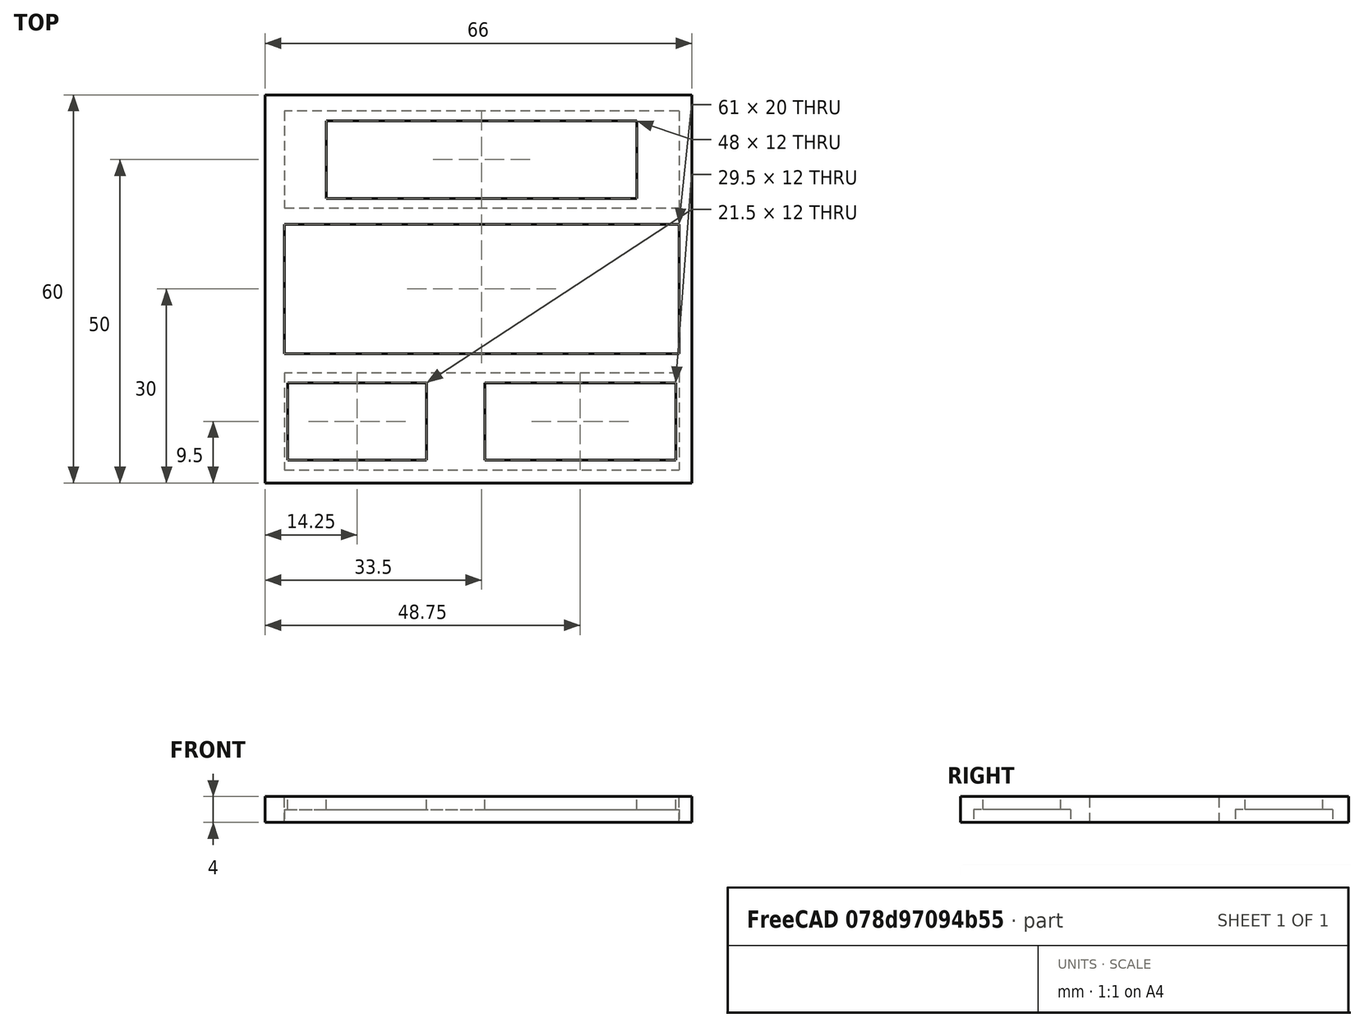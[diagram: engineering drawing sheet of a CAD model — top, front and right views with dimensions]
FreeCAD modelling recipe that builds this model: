
FCSTD DOCUMENT  (FreeCAD 0.17R13522 (Git))
Label: test_panel_display1
License: CreativeCommons Attribution-ShareAlike
LicenseURL: http://creativecommons.org/licenses/by-sa/4.0/
objects: Part::Feature×51, Part::Fuse×42, Part::Cut×22, Part::Part2DObjectPython×10, Part::Box×9, Part::FeaturePython×4, Part::Extrusion×1, App::DocumentObjectGroup×1
note: 139 computed .brp shape members not serialized (recipe doc carries the construction recipe); baked Part::Feature solids carry a one-line shape summary decoded from their .brp

FEATURE [Part::Box] Box  label="base principal"
  AttacherType = Attacher::AttachEngine3D
  Height = 4
  Length = 280
  Placement = pos=(0,0,-4) rot=(0,0,1;0rad)
  Width = 210
FEATURE [Part::Feature] Fusion008001001  label="perforador encoder"
  Placement = pos=(17,17,-6) rot=(1,0,0;3.14159rad)
  shape: bbox 82.5 x 15 x 10 mm, 18 faces (baked)
FEATURE [Part::Feature] Fusion008001001001  label="perforador active 1"
  Placement = pos=(17,98,-6) rot=(1,0,0;3.14159rad)
  shape: bbox 82.5 x 15 x 10 mm, 18 faces (baked)
FEATURE [Part::Feature] Fusion008001001002  label="perforador active 2"
  Placement = pos=(17,57.5,-6) rot=(1,0,0;3.14159rad)
  shape: bbox 82.5 x 15 x 10 mm, 18 faces (baked)
FEATURE [Part::Feature] Fusion008001001003  label="perforador standby 1"
  Placement = pos=(136,98,-6) rot=(1,0,0;3.14159rad)
  shape: bbox 82.5 x 15 x 10 mm, 18 faces (baked)
FEATURE [Part::Feature] Fusion008001001004  label="perforador standby 2"
  Placement = pos=(136,57.5,-6) rot=(1,0,0;3.14159rad)
  shape: bbox 82.5 x 15 x 10 mm, 18 faces (baked)
FEATURE [Part::Cut] Cut
  Base = -> Box
  Refine = true
  Tool = -> Fusion008001001
FEATURE [Part::Cut] Cut001
  Base = -> Cut
  Refine = true
  Tool = -> Fusion008001001001
FEATURE [Part::Cut] Cut002
  Base = -> Cut001
  Refine = true
  Tool = -> Fusion008001001002
FEATURE [Part::Cut] Cut003
  Base = -> Cut002
  Refine = true
  Tool = -> Fusion008001001003
FEATURE [Part::Cut] Cut004  label="base con 7 segmentos sin frente perforado"
  Base = -> Cut003
  Refine = true
  Tool = -> Fusion008001001004
FEATURE [Part::Feature] BooleanFragments001  label="perforador encoder izquierda"
  Placement = pos=(130,20.2,4) rot=(0,0,1;0rad)
  shape: bbox 45.2 x 30 x 10 mm, 34 faces, 4 solids (baked)
FEATURE [Part::Feature] BooleanFragments002  label="perforador encoder derecha"
  Placement = pos=(178,20.2,4) rot=(0,0,1;0rad)
  shape: bbox 45.2 x 30 x 10 mm, 34 faces, 4 solids (baked)
FEATURE [Part::Cut] Cut005
  Base = -> Cut004
  Refine = true
  Tool = -> BooleanFragments001
FEATURE [Part::Cut] Cut006  label="frente con agujeros displays y encoders transponder"
  Base = -> Cut005
  Refine = true
  Tool = -> BooleanFragments002
FEATURE [Part::Feature] Fusion005001  label="boton ident"
  Placement = pos=(203,14.2,1) rot=(0,0,1;0rad)
  shape: bbox 30 x 12 x 10 mm, 14 faces (baked)
FEATURE [Part::Cut] Cut007
  Base = -> Cut006
  Refine = true
  Tool = -> Fusion005001
FEATURE [Part::Part2DObjectPython] Line009  # Draft 2D object (typed FeaturePython)
  ChamferSize = 0
  Closed = false
  End = (270.847,20.2,0)
  FilletRadius = 0
  Length = 35.3471
  MakeFace = false
  Points = (2) [(235.5,20.2,0),(270.847,20.2,0)]
  Start = (235.5,20.2,0)
  Subdivisions = 0
FEATURE [Part::Part2DObjectPython] Circle  # Draft 2D object (typed FeaturePython)
  FirstAngle = 0
  LastAngle = 0
  MakeFace = false
  Placement = pos=(269.619,20.2,4) rot=(0,0,1;0rad)
  Radius = 4.75
FEATURE [Part::Part2DObjectPython] Circle001  # Draft 2D object (typed FeaturePython)
  FirstAngle = 0
  LastAngle = 0
  MakeFace = false
  Placement = pos=(259.67,20.2,0) rot=(0,0,1;0rad)
  Radius = 14
FEATURE [Part::Extrusion] Extrude
  Base = -> Circle
  Dir = (0,0,1)
  DirMode = 2
  FaceMakerClass = Part::FaceMakerBullseye
  LengthFwd = 10
  LengthRev = 0
  Placement = pos=(-10,0,-10) rot=(0,0,1;0rad)
  Solid = true
  Symmetric = false
FEATURE [Part::Part2DObjectPython] Line014  # Draft 2D object (typed FeaturePython)
  ChamferSize = 0
  Closed = false
  End = (248.272,28.2144,0)
  FilletRadius = 0
  Length = 13.696
  MakeFace = false
  Placement = pos=(-10,0,-4) rot=(0,0,1;0rad)
  Points = (2) [(269.378,20.2,4),(258.272,28.2144,4)]
  Start = (259.378,20.2,0)
  Subdivisions = 0
FEATURE [Part::Part2DObjectPython] Line015  # Draft 2D object (typed FeaturePython)
  ChamferSize = 0
  Closed = false
  End = (254.876,33.263,0)
  FilletRadius = 0
  Length = 13.7518
  MakeFace = false
  Placement = pos=(-10,0,-4) rot=(0,0,1;0rad)
  Points = (2) [(269.174,20.2,4),(264.876,33.263,4)]
  Start = (259.174,20.2,0)
  Subdivisions = 0
FEATURE [Part::Part2DObjectPython] Line016  # Draft 2D object (typed FeaturePython)
  ChamferSize = 0
  Closed = false
  End = (263.227,33.6931,0)
  FilletRadius = 0
  Length = 14.1488
  MakeFace = false
  Placement = pos=(-10,0,-4) rot=(0,0,1;0rad)
  Points = (2) [(268.97,20.2,4),(273.227,33.6931,4)]
  Start = (258.97,20.2,0)
  Subdivisions = 0
FEATURE [Part::Part2DObjectPython] Line017  # Draft 2D object (typed FeaturePython)
  ChamferSize = 0
  Closed = false
  End = (270.612,28.9289,0)
  FilletRadius = 0
  Length = 14.5511
  MakeFace = false
  Placement = pos=(-10,0,-4) rot=(0,0,1;0rad)
  Points = (2) [(268.97,20.2,4),(280.612,28.9289,4)]
  Start = (258.97,20.2,0)
  Subdivisions = 0
FEATURE [Part::Part2DObjectPython] Line  # Draft 2D object (typed FeaturePython)
  ChamferSize = 0
  Closed = true
  End = (269.619,20.2,0)
  FilletRadius = 0
  Length = 0
  MakeFace = false
  Points = (2) [(269.619,20.2,0),(269.619,20.2,0)]
  Start = (269.619,20.2,0)
  Subdivisions = 0
FEATURE [Part::Cut] Cut008  label="base con line inferior completa"
  Base = -> Cut007
  Refine = true
  Tool = -> Extrude
FEATURE [Part::Part2DObjectPython] Line019  # Draft 2D object (typed FeaturePython)
  ChamferSize = 0
  Closed = false
  End = (259.619,169.66,0)
  FilletRadius = 0
  Length = 149.46
  MakeFace = true
  Placement = pos=(-20,0,-10) rot=(0,0,1;0rad)
  Points = (2) [(279.619,20.2,10),(279.619,169.66,10)]
  Start = (259.619,20.2,0)
  Subdivisions = 0
FEATURE [Part::Part2DObjectPython] Line023  # Draft 2D object (typed FeaturePython)
  ChamferSize = 0
  Closed = false
  End = (270.85,61,0)
  FilletRadius = 0
  Length = 96.85
  MakeFace = false
  Points = (2) [(174,61,0),(270.85,61,0)]
  Start = (174,61,0)
  Subdivisions = 0
FEATURE [App::DocumentObjectGroup] Construction
  Group = -> [Line009,Circle001,Line014,Line015,Line016,Line017,Line,Line019,Line023]
FEATURE [Part::Feature] BooleanFragments003  label="perforador para comunication 1"
  Placement = pos=(251.8,102,3) rot=(0,0,1;3.14159rad)
  shape: bbox 45.2 x 30 x 10 mm, 34 faces, 4 solids (baked)
FEATURE [Part::Feature] BooleanFragments003001  label="perforador para comunication 2"
  Placement = pos=(251.8,61,4) rot=(0,0,1;3.14159rad)
  shape: bbox 45.2 x 30 x 10 mm, 34 faces, 4 solids (baked)
FEATURE [Part::Cut] Cut009
  Base = -> Cut008
  Refine = true
  Tool = -> BooleanFragments003001
FEATURE [Part::Cut] Cut010  label="panel sin botones y sin leds"
  Base = -> Cut009
  Refine = true
  Tool = -> BooleanFragments003
FEATURE [Part::Feature] Cut001001  label="the_spacer_1mm_inside"
  Placement = pos=(17,106.2,0) rot=(0.99953,0.030644,0;3.14159rad)
  shape: bbox 7 x 7 x 6 mm, 11 faces (baked)
FEATURE [Part::Fuse] Fusion
  Base = -> Cut010
  Refine = true
  Tool = -> Cut001001
FEATURE [Part::Fuse] Fusion008001001005
  Base = -> Fusion
  Refine = true
FEATURE [Part::Feature] Cut001001001  label="the_spacer_1mm_inside001"
  Placement = pos=(17,96.8,0) rot=(0.99953,0.030644,0;3.14159rad)
  shape: bbox 7 x 7 x 6 mm, 11 faces (baked)
FEATURE [Part::Fuse] Fusion008001001006
  Base = -> Fusion008001001005
  Refine = true
  Tool = -> Cut001001001
FEATURE [Part::Fuse] Fusion008001001007
  Placement = pos=(0,0,1) rot=(0,0,1;0rad)
  Refine = true
  Tool = -> Fusion008001001006
FEATURE [Part::Feature] Cut001001001001  label="the_spacer_1mm_inside002"
  Placement = pos=(17,56.3,0) rot=(0.99953,0.030644,0;3.14159rad)
  shape: bbox 7 x 7 x 6 mm, 11 faces (baked)
FEATURE [Part::Feature] Cut001001001002  label="the_spacer_1mm_inside003"
  Placement = pos=(17,65.7,0) rot=(0.99953,0.030644,0;3.14159rad)
  shape: bbox 7 x 7 x 6 mm, 11 faces (baked)
FEATURE [Part::Feature] Cut001001001002001  label="the_spacer_1mm_inside004"
  Placement = pos=(17,25.2,0) rot=(0.99953,0.030644,0;3.14159rad)
  shape: bbox 7 x 7 x 6 mm, 11 faces (baked)
FEATURE [Part::Feature] Cut001001001001001  label="the_spacer_1mm_inside005"
  Placement = pos=(17,15.8,0) rot=(0.99953,0.030644,0;3.14159rad)
  shape: bbox 7 x 7 x 6 mm, 11 faces (baked)
FEATURE [Part::Feature] Cut001001001002002  label="the_spacer_1mm_inside006"
  Placement = pos=(136,106.2,0) rot=(0.99953,0.030644,0;3.14159rad)
  shape: bbox 7 x 7 x 6 mm, 11 faces (baked)
FEATURE [Part::Feature] Cut001001001002003  label="the_spacer_1mm_inside007"
  Placement = pos=(136,96.8,0) rot=(0.99953,0.030644,0;3.14159rad)
  shape: bbox 7 x 7 x 6 mm, 11 faces (baked)
FEATURE [Part::Feature] Cut001001001002004  label="the_spacer_1mm_inside008"
  Placement = pos=(136,65.7,0) rot=(0.99953,0.030644,0;3.14159rad)
  shape: bbox 7 x 7 x 6 mm, 11 faces (baked)
FEATURE [Part::Feature] Cut001001001001002  label="the_spacer_1mm_inside009"
  Placement = pos=(136,56.3,0) rot=(0.99953,0.030644,0;3.14159rad)
  shape: bbox 7 x 7 x 6 mm, 11 faces (baked)
FEATURE [Part::Feature] Cut001001001001002001  label="the_spacer_1mm_inside010"
  Placement = pos=(93,65.7,0) rot=(0.99953,0.030644,0;3.14159rad)
  shape: bbox 7 x 7 x 6 mm, 11 faces (baked)
FEATURE [Part::Feature] Cut001001001002002001  label="the_spacer_1mm_inside011"
  Placement = pos=(93,106.2,0) rot=(0.99953,0.030644,0;3.14159rad)
  shape: bbox 7 x 7 x 6 mm, 11 faces (baked)
FEATURE [Part::Feature] Cut001001001002003001  label="the_spacer_1mm_inside012"
  Placement = pos=(93,96.8,0) rot=(0.99953,0.030644,0;3.14159rad)
  shape: bbox 7 x 7 x 6 mm, 11 faces (baked)
FEATURE [Part::Feature] Cut001001001001002002  label="the_spacer_1mm_inside013"
  Placement = pos=(93,56.3,0) rot=(0.99953,0.030644,0;3.14159rad)
  shape: bbox 7 x 7 x 6 mm, 11 faces (baked)
FEATURE [Part::Feature] Cut001001001002001001  label="the_spacer_1mm_inside014"
  Placement = pos=(93,25.2,0) rot=(0.99953,0.030644,0;3.14159rad)
  shape: bbox 7 x 7 x 6 mm, 11 faces (baked)
FEATURE [Part::Feature] Cut001001001001001001  label="the_spacer_1mm_inside015"
  Placement = pos=(93,15.8,0) rot=(0.99953,0.030644,0;3.14159rad)
  shape: bbox 7 x 7 x 6 mm, 11 faces (baked)
FEATURE [Part::Feature] Cut001001001002002001001  label="the_spacer_1mm_inside016"
  Placement = pos=(212,106.2,0) rot=(0.99953,0.030644,0;3.14159rad)
  shape: bbox 7 x 7 x 6 mm, 11 faces (baked)
FEATURE [Part::Feature] Cut001001001002003001001  label="the_spacer_1mm_inside017"
  Placement = pos=(212,96.8,0) rot=(0.99953,0.030644,0;3.14159rad)
  shape: bbox 7 x 7 x 6 mm, 11 faces (baked)
FEATURE [Part::Feature] Cut001001001001002001001  label="the_spacer_1mm_inside018"
  Placement = pos=(212,65.7,0) rot=(0.99953,0.030644,0;3.14159rad)
  shape: bbox 7 x 7 x 6 mm, 11 faces (baked)
FEATURE [Part::Feature] Cut001001001001002002001  label="the_spacer_1mm_inside019"
  Placement = pos=(212,56.3,0) rot=(0.99953,0.030644,0;3.14159rad)
  shape: bbox 7 x 7 x 6 mm, 11 faces (baked)
FEATURE [Part::Fuse] Fusion008001001008
  Base = -> Cut001001001001
  Refine = true
  Tool = -> Cut001001001002
FEATURE [Part::Fuse] Fusion008001001009
  Base = -> Cut001001001002001
  Refine = true
  Tool = -> Cut001001001001001
FEATURE [Part::Fuse] Fusion008001001010
  Base = -> Cut001001001002002001
  Refine = true
  Tool = -> Cut001001001002003001
FEATURE [Part::Fuse] Fusion008001001011
  Base = -> Cut001001001002002001
  Refine = true
  Tool = -> Cut001001001002003001
FEATURE [Part::Fuse] Fusion008001001012
  Base = -> Cut001001001001002001
  Refine = true
  Tool = -> Cut001001001001002002
FEATURE [Part::Fuse] Fusion008001001013
  Base = -> Cut001001001002001001
  Refine = true
  Tool = -> Cut001001001001001001
FEATURE [Part::Fuse] Fusion008001001014
  Base = -> Cut001001001002002
  Refine = true
  Tool = -> Cut001001001002003
FEATURE [Part::Fuse] Fusion008001001015
  Base = -> Cut001001001002002
  Refine = true
  Tool = -> Cut001001001002003
FEATURE [Part::Fuse] Fusion008001001016
  Base = -> Cut001001001002004
  Refine = true
  Tool = -> Cut001001001001002
FEATURE [Part::Fuse] Fusion008001001017
  Base = -> Cut001001001002002001001
  Refine = true
  Tool = -> Cut001001001002003001001
FEATURE [Part::Fuse] Fusion008001001018
  Base = -> Cut001001001001002001001
  Refine = true
  Tool = -> Cut001001001001002002001
FEATURE [Part::FeaturePython] BooleanFragments  # WARN: FeaturePython — macro-defined, semantics opaque (R4)
  Mode = 0
  Objects = -> [Fusion008001001007,Fusion008001001008]
  Tolerance = 0
FEATURE [Part::FeaturePython] BooleanFragments003002  # WARN: FeaturePython — macro-defined, semantics opaque (R4)
  Mode = 0
  Objects = -> [BooleanFragments,Fusion008001001009]
  Tolerance = 0
FEATURE [Part::FeaturePython] BooleanFragments003003  # WARN: FeaturePython — macro-defined, semantics opaque (R4)
  Mode = 0
  Objects = -> [BooleanFragments003002,Fusion008001001010]
  Tolerance = 0
FEATURE [Part::FeaturePython] BooleanFragments003004  # WARN: FeaturePython — macro-defined, semantics opaque (R4)
  Mode = 0
  Objects = -> [BooleanFragments003003,Fusion008001001012]
  Tolerance = 0
FEATURE [Part::Fuse] Fusion008001001019
  Base = -> Fusion008001001013
  Refine = true
  Tool = -> BooleanFragments003004
FEATURE [Part::Fuse] Fusion008001001020
  Base = -> Fusion008001001014
  Refine = true
  Tool = -> Fusion008001001019
FEATURE [Part::Fuse] Fusion008001001021
  Base = -> Fusion008001001014
  Refine = true
  Tool = -> Fusion008001001019
FEATURE [Part::Fuse] Fusion008001001022
  Base = -> Fusion008001001011
  Refine = true
  Tool = -> Fusion008001001020
FEATURE [Part::Fuse] Fusion008001001023
  Base = -> Fusion008001001021
  Refine = true
  Tool = -> Fusion008001001022
FEATURE [Part::Fuse] Fusion008001001024
  Base = -> Fusion008001001016
  Refine = true
  Tool = -> Fusion008001001023
FEATURE [Part::Fuse] Fusion008001001025
  Base = -> Fusion008001001017
  Refine = true
  Tool = -> Fusion008001001024
FEATURE [Part::Fuse] Fusion008001001026
  Base = -> Fusion008001001018
  Refine = true
  Tool = -> Fusion008001001025
FEATURE [Part::Fuse] Fusion008001001027
  Base = -> Fusion008001001015
  Refine = true
  Tool = -> Fusion008001001026
FEATURE [Part::Feature] Box001001001  label="Cube002"
  Placement = pos=(14,53.5,-2) rot=(0,0,1;0rad)
  shape: bbox 6 x 6 x 3 mm, 6 faces (baked)
FEATURE [Part::Feature] Box001001002  label="Cube003"
  Placement = pos=(14,62.5,-2) rot=(0,0,1;0rad)
  shape: bbox 6 x 6 x 3 mm, 6 faces (baked)
FEATURE [Part::Feature] Box001001001001  label="Cube004"
  Placement = pos=(14,13,-2) rot=(0,0,1;0rad)
  shape: bbox 6 x 6 x 3 mm, 6 faces (baked)
FEATURE [Part::Feature] Box001001002001  label="Cube005"
  Placement = pos=(14,22,-2) rot=(0,0,1;0rad)
  shape: bbox 6 x 6 x 3 mm, 6 faces (baked)
FEATURE [Part::Feature] Box001001002002  label="Cube006"
  Placement = pos=(133,62.5,-2) rot=(0,0,1;0rad)
  shape: bbox 6 x 6 x 3 mm, 6 faces (baked)
FEATURE [Part::Feature] Box001001001002  label="Cube007"
  Placement = pos=(133,53.5,-2) rot=(0,0,1;0rad)
  shape: bbox 6 x 6 x 3 mm, 6 faces (baked)
FEATURE [Part::Feature] Box001001002002001  label="Cube008"
  Placement = pos=(133,103,-2) rot=(0,0,1;0rad)
  shape: bbox 6 x 6 x 3 mm, 6 faces (baked)
FEATURE [Part::Feature] Box001001001002001  label="Cube009"
  Placement = pos=(133,94,-2) rot=(0,0,1;0rad)
  shape: bbox 6 x 6 x 3 mm, 6 faces (baked)
FEATURE [Part::Fuse] Fusion008001001028
  Base = -> Fusion008001001027
  Refine = true
  Tool = -> Box001001001001
FEATURE [Part::Fuse] Fusion008001001029
  Base = -> Box001001002001
  Refine = true
  Tool = -> Fusion008001001028
FEATURE [Part::Fuse] Fusion008001001030
  Base = -> Box001001001002001
  Refine = true
  Tool = -> Fusion008001001029
FEATURE [Part::Fuse] Fusion008001001031
  Base = -> Box001001002002001
  Refine = true
  Tool = -> Fusion008001001030
FEATURE [Part::Feature] Box001001001002002  label="Cube010"
  Placement = pos=(90,53.5,-2) rot=(0,0,1;0rad)
  shape: bbox 6 x 6 x 3 mm, 6 faces (baked)
FEATURE [Part::Feature] Box001001002002002  label="Cube011"
  Placement = pos=(90,62.5,-2) rot=(0,0,1;0rad)
  shape: bbox 6 x 6 x 3 mm, 6 faces (baked)
FEATURE [Part::Feature] Box001001001002003  label="Cube012"
  Placement = pos=(209,54.5,-2) rot=(0,0,1;0rad)
  shape: bbox 6 x 6 x 3 mm, 6 faces (baked)
FEATURE [Part::Feature] Box001001002002002001  label="Cube013"
  Placement = pos=(209,62.5,-2) rot=(0,0,1;0rad)
  shape: bbox 6 x 6 x 3 mm, 6 faces (baked)
FEATURE [Part::Feature] Box001001001002002001  label="Cube014"
  Placement = pos=(90,13.5,-2) rot=(0,0,1;0rad)
  shape: bbox 6 x 6 x 3 mm, 6 faces (baked)
FEATURE [Part::Feature] Box001001002002002002  label="Cube015"
  Placement = pos=(90,22.5,-2) rot=(0,0,1;0rad)
  shape: bbox 6 x 6 x 3 mm, 6 faces (baked)
FEATURE [Part::Fuse] Fusion008001001032
  Base = -> Fusion008001001031
  Refine = true
  Tool = -> Box001001002002002002
FEATURE [Part::Fuse] Fusion008001001033
  Base = -> Box001001001002002001
  Refine = true
  Tool = -> Fusion008001001032
FEATURE [Part::Fuse] Fusion008001001034
  Base = -> Box001001001
  Refine = true
  Tool = -> Fusion008001001033
FEATURE [Part::Fuse] Fusion008001001035
  Base = -> Box001001002
  Refine = true
  Tool = -> Fusion008001001034
FEATURE [Part::Fuse] Fusion008001001036
  Base = -> Box001001001002
  Refine = true
  Tool = -> Fusion008001001035
FEATURE [Part::Fuse] Fusion008001001037
  Base = -> Box001001002002
  Refine = true
  Tool = -> Fusion008001001036
FEATURE [Part::Feature] Box001001002002002001001  label="Cube016"
  Placement = pos=(209,103.5,-2) rot=(0,0,1;0rad)
  shape: bbox 6 x 6 x 3 mm, 6 faces (baked)
FEATURE [Part::Fuse] Fusion008001001038
  Base = -> Box001001002002002001
  Refine = true
  Tool = -> Fusion008001001037
FEATURE [Part::Feature] Box001001001002003001  label="Cube017"
  Placement = pos=(209,94.5,-2) rot=(0,0,1;0rad)
  shape: bbox 6 x 6 x 3 mm, 6 faces (baked)
FEATURE [Part::Fuse] Fusion008001001039
  Base = -> Box001001001002003
  Refine = true
  Tool = -> Fusion008001001038
FEATURE [Part::Fuse] Fusion008001001040
  Base = -> Box001001001002003001
  Refine = true
  Tool = -> Fusion008001001039
FEATURE [Part::Fuse] Fusion008001001041
  Base = -> Box001001002002002001001
  Refine = true
  Tool = -> Fusion008001001040
FEATURE [Part::Feature] Box001001001002002002  label="Cube018"
  Placement = pos=(90,94.5,-2) rot=(0,0,1;0rad)
  shape: bbox 6 x 6 x 3 mm, 6 faces (baked)
FEATURE [Part::Fuse] Fusion008001001042
  Base = -> Box001001001002002
  Refine = true
  Tool = -> Fusion008001001041
FEATURE [Part::Fuse] Fusion008001001043
  Base = -> Box001001001002002002
  Refine = true
  Tool = -> Fusion008001001042
FEATURE [Part::Feature] Box001001002002002001002  label="Cube019"
  Placement = pos=(90,103.5,-2) rot=(0,0,1;0rad)
  shape: bbox 6 x 6 x 3 mm, 6 faces (baked)
FEATURE [Part::Fuse] Fusion008001001044
  Base = -> Box001001002002002
  Refine = true
  Tool = -> Fusion008001001043
FEATURE [Part::Fuse] Fusion008001001045
  Base = -> Box001001002002002001002
  Refine = true
  Tool = -> Fusion008001001044
FEATURE [Part::Box] Box001001002002002001003  label="Cube020"
  AttacherType = Attacher::AttachEngine3D
  Height = 20
  Length = 48
  Placement = pos=(32.5,55,-5) rot=(0,0,1;0rad)
  Width = 12
FEATURE [Part::Feature] Box001001002002002001003001  label="Cube021"
  Placement = pos=(32.5,95.5,-5) rot=(0,0,1;0rad)
  shape: bbox 48 x 12 x 20 mm, 6 faces (baked)
FEATURE [Part::Feature] Box001001002002002001003001001  label="Cube022"
  Placement = pos=(151.5,95.5,-5) rot=(0,0,1;0rad)
  shape: bbox 48 x 12 x 20 mm, 6 faces (baked)
FEATURE [Part::Feature] Box001001002002002001003001001001  label="Cube023"
  Placement = pos=(151.5,55,-5) rot=(0,0,1;0rad)
  shape: bbox 48 x 12 x 20 mm, 6 faces (baked)
FEATURE [Part::Cut] Cut001001001002003001002
  Base = -> Fusion008001001045
  Refine = true
  Tool = -> Box001001002002002001003001001001
FEATURE [Part::Cut] Cut001001001002003001003
  Base = -> Cut001001001002003001002
  Refine = true
  Tool = -> Box001001002002002001003001001
FEATURE [Part::Cut] Cut001001001002003001004
  Base = -> Cut001001001002003001003
  Refine = true
  Tool = -> Box001001002002002001003001
FEATURE [Part::Cut] Cut001001001002003001005
  Base = -> Cut001001001002003001004
  Refine = true
  Tool = -> Box001001002002002001003
FEATURE [Part::Box] Box001001002002002001003001001002  label="Cube024"
  AttacherType = Attacher::AttachEngine3D
  Height = 30
  Length = 21.5
  Placement = pos=(26.5,14.5,-12) rot=(0,0,1;0rad)
  Width = 12
FEATURE [Part::Box] Box001001002002002001003001001003  label="Cube025"
  AttacherType = Attacher::AttachEngine3D
  Height = 30
  Length = 29.5
  Placement = pos=(57,14.5,-12) rot=(0,0,1;0rad)
  Width = 12
FEATURE [Part::Cut] Cut001001001002003001006
  Base = -> Cut001001001002003001005
  Refine = true
  Tool = -> Box001001002002002001003001001002
FEATURE [Part::Cut] Cut001001001002003001007  label="panel con 5 displayes y sus spacers"
  Base = -> Cut001001001002003001006
  Refine = true
  Tool = -> Box001001002002002001003001001003
FEATURE [Part::Box] Box001001002002002001003001001004  label="Cube026"
  AttacherType = Attacher::AttachEngine3D
  Height = 30
  Length = 300
  Placement = pos=(-7,71,-12) rot=(0,0,1;0rad)
  Width = 200
FEATURE [Part::Cut] Cut001001001002003001008
  Base = -> Cut001001001002003001007
  Refine = true
  Tool = -> Box001001002002002001003001001004
FEATURE [Part::Box] Box001001002002002001003001001005  label="Cube027"
  AttacherType = Attacher::AttachEngine3D
  Height = 30
  Length = 300
  Placement = pos=(89,-19,-12) rot=(0,0,1;0rad)
  Width = 200
FEATURE [Part::Cut] Cut001001001002003001009
  Base = -> Cut001001001002003001008
  Refine = true
  Tool = -> Box001001002002002001003001001005
FEATURE [Part::Box] Box001001002002002001003001001006  label="Cube028"
  AttacherType = Attacher::AttachEngine3D
  Height = 60
  Length = 50
  Placement = pos=(-27,-15,-14) rot=(0,0,1;0rad)
  Width = 200
FEATURE [Part::Cut] Cut001001001002003001010
  Base = -> Cut001001001002003001009
  Refine = true
  Tool = -> Box001001002002002001003001001006
FEATURE [Part::Box] Box001001002002002001003001001007  label="Cube"
  AttacherType = Attacher::AttachEngine3D
  Height = 30
  Length = 61
  Placement = pos=(26,31,-16) rot=(0,0,1;0rad)
  Width = 20
FEATURE [Part::Cut] Cut001001001002003001011
  Base = -> Cut001001001002003001010
  Refine = true
  Tool = -> Box001001002002002001003001001007
FEATURE [Part::Box] Box001001002002002001003001001008  label="Cube029"
  AttacherType = Attacher::AttachEngine3D
  Height = 28
  Length = 92
  Placement = pos=(6,-4,-10) rot=(0,0,1;0rad)
  Width = 15
FEATURE [Part::Cut] Cut001001001002003001012
  Base = -> Cut001001001002003001011
  Refine = true
  Tool = -> Box001001002002002001003001001008
